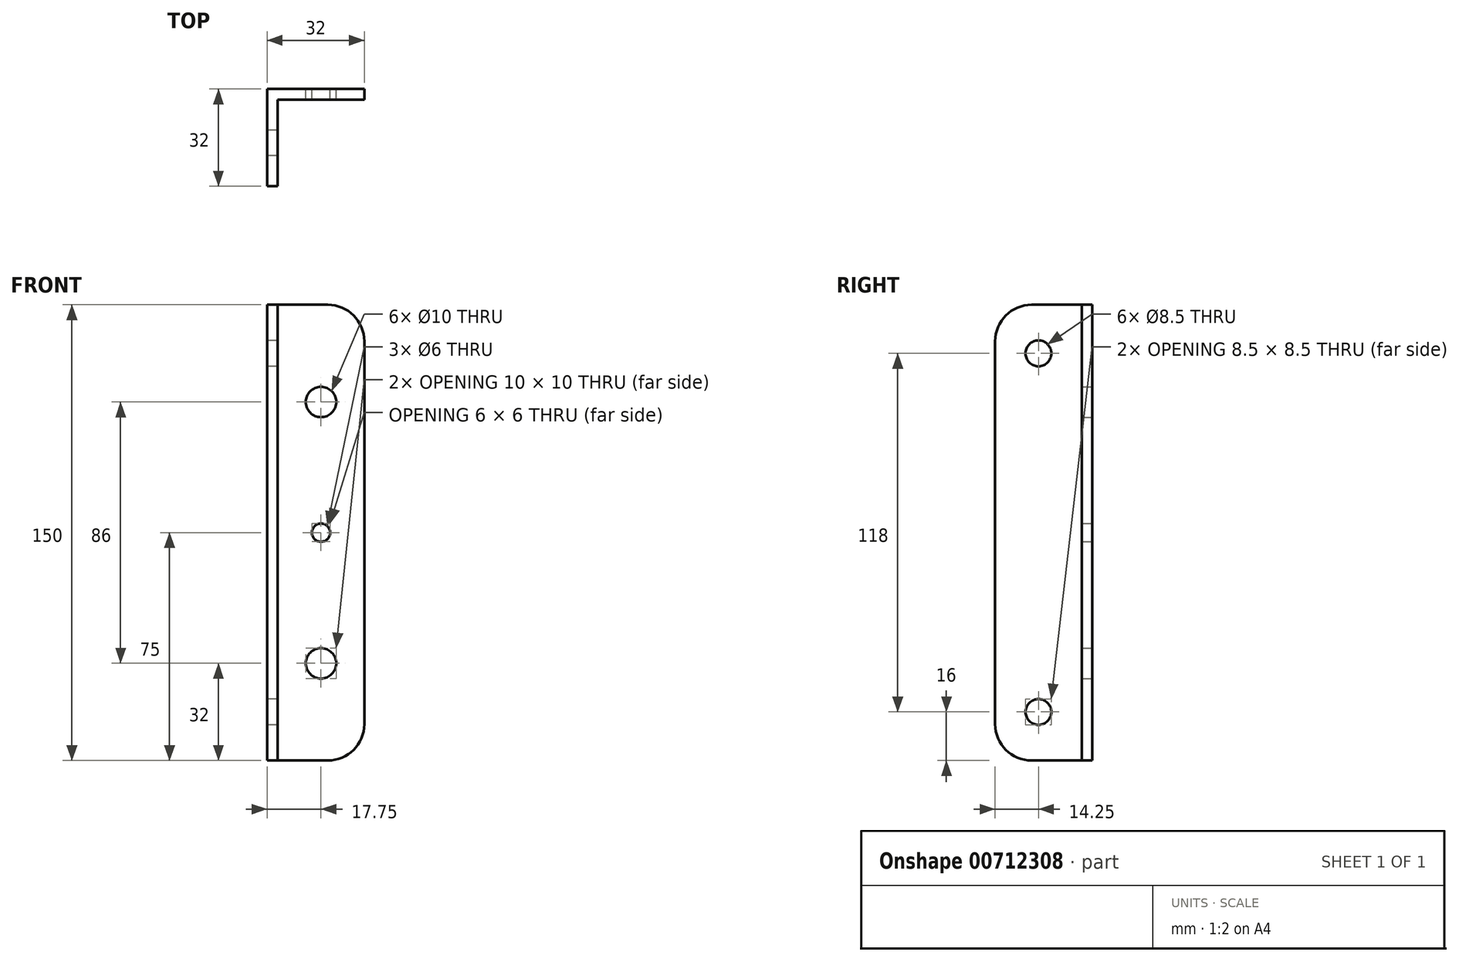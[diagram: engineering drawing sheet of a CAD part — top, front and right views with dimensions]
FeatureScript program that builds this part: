
annotation { "Feature Type Name" : "Feature", "Feature Type Description" : "" }
export const myFeature = defineFeature(function(context is Context, id is Id, definition is map)
    precondition{}
    {
        {
            var Q0;
            Q0=qCreatedBy(makeId("Top.planeOp"),FACE);
            var sketch = newSketch(context, id + "F0", { "sketchPlane" : qUnion([Q0])});
            skLineSegment(sketch, "E0", {"start": v(32, 0) * mm, "end": v(0, 0) * mm});
            skLineSegment(sketch, "E1", {"start": v(0, 0) * mm, "end": v(0, -32) * mm});
            skLineSegment(sketch, "E2", {"start": v(0, -32) * mm, "end": v(3.5, -32) * mm});
            skLineSegment(sketch, "E3", {"start": v(3.5, -32) * mm, "end": v(3.5, -3.5) * mm});
            skLineSegment(sketch, "E4", {"start": v(3.5, -3.5) * mm, "end": v(32, -3.5) * mm});
            skLineSegment(sketch, "E5", {"start": v(32, -3.5) * mm, "end": v(32, 0) * mm});
            skSolve(sketch);
        }
        {
            var Q0;
            Q0 = qSketchRegion(id + "F0", true);
            extrude(context, id + "F1", {"entities" : qUnion([Q0]), "depth" : 150 * mm, "offsetDistance" : 25 * mm});
        }
        {
            var Q0;
            Q0=makeQuery(id+"F1.opExtrude","SWEPT_FACE",FACE,{"disambiguationData":[OSD([sQuery(id+"F0.wireOp",EDGE,"E3")])]});
            var sketch = newSketch(context, id + "F2", { "sketchPlane" : qUnion([Q0])});
            skLineSegment(sketch, "E6", {"start": v(-17.75, 150) * mm, "end": v(-17.75, 0) * mm, "construction": true});
            skPoint(sketch, "E7", {"position": v(-17.75, 134) * mm});
            skPoint(sketch, "E8", {"position": v(-17.75, 16) * mm});
            skSolve(sketch);
        }
        {
            var Q0;
            Q0=sQuery(id+"F2.wireOp",VERTEX,"E7");
            var Q1;
            Q1=sQuery(id+"F2.wireOp",VERTEX,"E8");
            var Q2;
            Q2=makeQuery(id+"F1.opExtrude","SWEPT_BODY",BODY,{"disambiguationData":[OSD([sQuery(id+"F0.wireOp",EDGE,"E0"),sQuery(id+"F0.wireOp",EDGE,"E1"),sQuery(id+"F0.wireOp",EDGE,"E2"),sQuery(id+"F0.wireOp",EDGE,"E3"),sQuery(id+"F0.wireOp",EDGE,"E4"),sQuery(id+"F0.wireOp",EDGE,"E5")])]});
            hole(context, id + "F3", {"style" : HoleStyle.SIMPLE, "endStyle" : HoleEndStyle.BLIND, "standardTappedOrClearance" : lookupTablePath({ "standard" : "ISO", "engagement" : "75%", "pitch" : "1.5 mm", "size" : "M10", "type" : "Tapped" }), "standardBlindInLast" : lookupTablePath({ "standard" : "ISO", "engagement" : "75%", "pitch" : "1.5 mm", "size" : "M10", "type" : "Tapped" }), "holeDiameter" : 8.5 * mm, "majorDiameter" : 10 * mm, "showTappedDepth" : true, "holeDepth" : 16.5 * mm, "isTappedThrough" : true, "tappedDepth" : 12 * mm, "tapClearance" : 3, "locations" : qUnion([Q0, Q1]), "scope" : qUnion([Q2]), "startStyle" : HoleStartStyle.PART});
        }
        {
            var Q0;
            Q0=makeQuery(id+"F1.opExtrude","SWEPT_FACE",FACE,{"disambiguationData":[OSD([sQuery(id+"F0.wireOp",EDGE,"E4")])]});
            var sketch = newSketch(context, id + "F4", { "sketchPlane" : qUnion([Q0])});
            skLineSegment(sketch, "E9", {"start": v(17.75, 150) * mm, "end": v(17.75, 0) * mm, "construction": true});
            skPoint(sketch, "E10", {"position": v(17.75, 118) * mm});
            skPoint(sketch, "E11", {"position": v(17.75, 32) * mm});
            skPoint(sketch, "E12", {"position": v(17.75, 75) * mm});
            skSolve(sketch);
        }
        {
            var Q0;
            Q0=sQuery(id+"F4.wireOp",VERTEX,"E10");
            var Q1;
            Q1=sQuery(id+"F4.wireOp",VERTEX,"E11");
            var Q2;
            Q2=makeQuery(id+"F1.opExtrude","SWEPT_BODY",BODY,{"disambiguationData":[OSD([sQuery(id+"F0.wireOp",EDGE,"E0"),sQuery(id+"F0.wireOp",EDGE,"E1"),sQuery(id+"F0.wireOp",EDGE,"E2"),sQuery(id+"F0.wireOp",EDGE,"E3"),sQuery(id+"F0.wireOp",EDGE,"E4"),sQuery(id+"F0.wireOp",EDGE,"E5")])]});
            hole(context, id + "F5", {"style" : HoleStyle.SIMPLE, "endStyle" : HoleEndStyle.BLIND, "holeDiameter" : 10 * mm, "majorDiameter" : 5 * mm, "holeDepth" : 25 * mm, "isTappedThrough" : true, "tappedDepth" : 12 * mm, "tapClearance" : 3, "locations" : qUnion([Q0, Q1]), "scope" : qUnion([Q2]), "startStyle" : HoleStartStyle.PART});
        }
        {
            var Q0;
            Q0=makeQuery(id+"F1.opExtrude","SWEPT_FACE",FACE,{"disambiguationData":[OSD([sQuery(id+"F0.wireOp",EDGE,"E4")])]});
            var sketch = newSketch(context, id + "F6", { "sketchPlane" : qUnion([Q0])});
            skLineSegment(sketch, "E13", {"start": v(17.75, 150) * mm, "end": v(17.75, 0) * mm, "construction": true});
            skPoint(sketch, "E14", {"position": v(17.75, 75) * mm});
            skSolve(sketch);
        }
        {
            var Q0;
            Q0=sQuery(id+"F6.wireOp",VERTEX,"E14");
            var Q1;
            Q1=makeQuery(id+"F1.opExtrude","SWEPT_BODY",BODY,{"disambiguationData":[OSD([sQuery(id+"F0.wireOp",EDGE,"E0"),sQuery(id+"F0.wireOp",EDGE,"E1"),sQuery(id+"F0.wireOp",EDGE,"E2"),sQuery(id+"F0.wireOp",EDGE,"E3"),sQuery(id+"F0.wireOp",EDGE,"E4"),sQuery(id+"F0.wireOp",EDGE,"E5")])]});
            hole(context, id + "F7", {"style" : HoleStyle.SIMPLE, "endStyle" : HoleEndStyle.BLIND, "holeDiameter" : 6 * mm, "majorDiameter" : 5 * mm, "holeDepth" : 25 * mm, "isTappedThrough" : true, "tappedDepth" : 12 * mm, "tapClearance" : 3, "locations" : qUnion([Q0]), "scope" : qUnion([Q1]), "startStyle" : HoleStartStyle.PART});
        }
        {
            var Q0;
            Q0=makeQuery(id+"F1.opExtrude","CAP_EDGE",EDGE,{"disambiguationData":[OSD([sQuery(id+"F0.wireOp",EDGE,"E2")])],"isStart":false});
            var Q1;
            Q1=makeQuery(id+"F1.opExtrude","CAP_EDGE",EDGE,{"disambiguationData":[OSD([sQuery(id+"F0.wireOp",EDGE,"E5")])],"isStart":false});
            var Q2;
            Q2=makeQuery(id+"F1.opExtrude","CAP_EDGE",EDGE,{"disambiguationData":[OSD([sQuery(id+"F0.wireOp",EDGE,"E5")])],"isStart":true});
            var Q3;
            Q3=makeQuery(id+"F1.opExtrude","CAP_EDGE",EDGE,{"disambiguationData":[OSD([sQuery(id+"F0.wireOp",EDGE,"E2")])],"isStart":true});
            fillet(context, id + "F8", {"entities" : qUnion([Q0, Q1, Q2, Q3]), "radius" : 12 * mm, "tangentPropagation" : true, "allowEdgeOverflow" : false});
        }
    });
